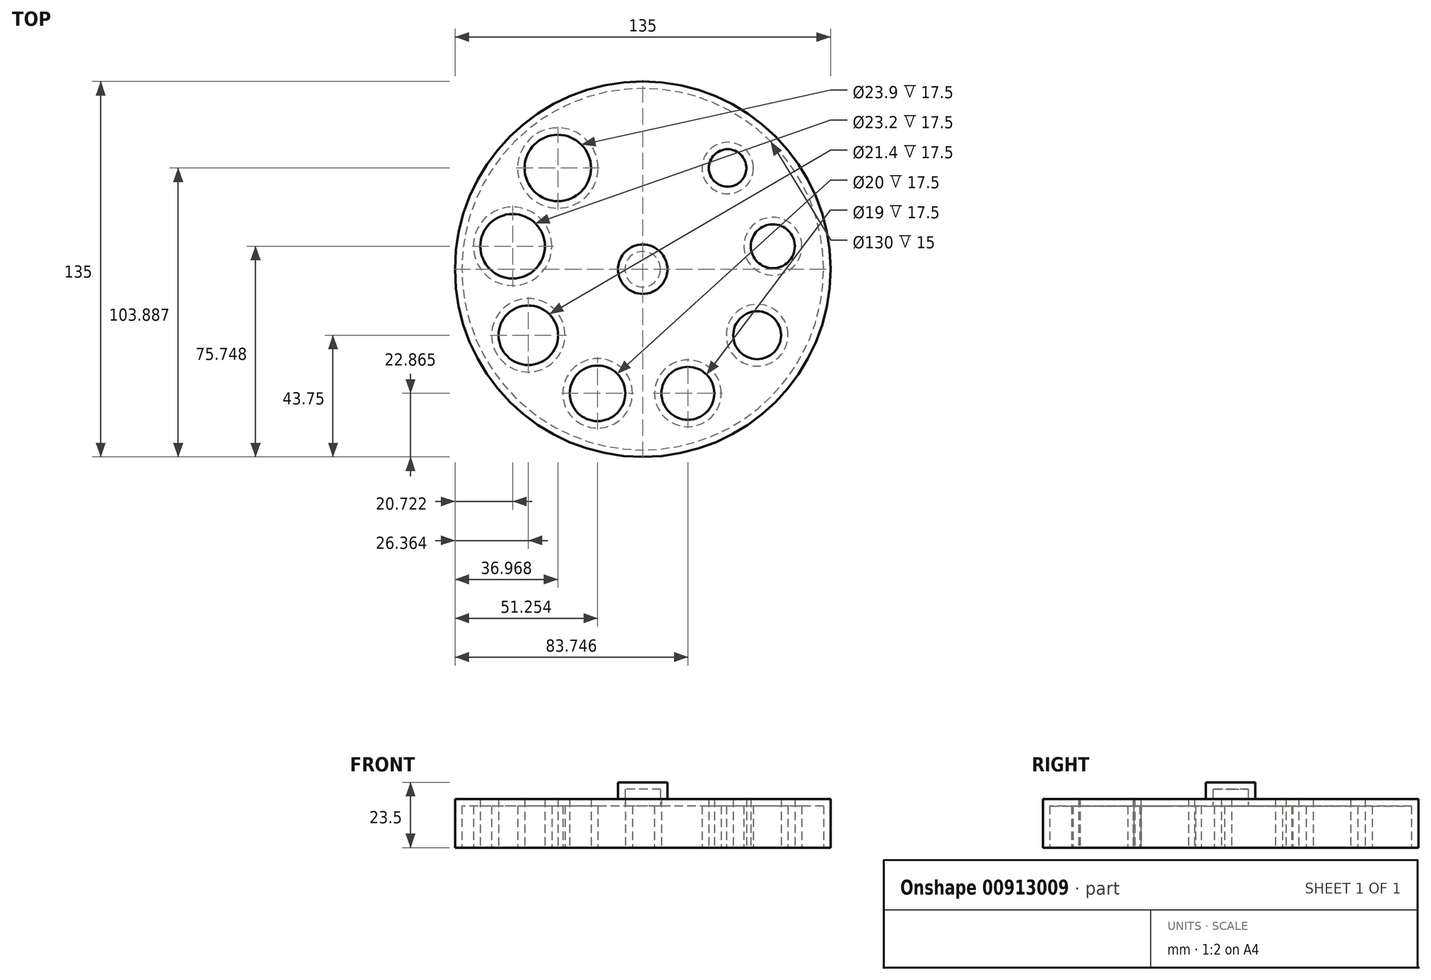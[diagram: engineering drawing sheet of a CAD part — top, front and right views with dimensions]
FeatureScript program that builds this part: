
annotation { "Feature Type Name" : "Feature", "Feature Type Description" : "" }
export const myFeature = defineFeature(function(context is Context, id is Id, definition is map)
    precondition{}
    {
        {
            var Q0;
            Q0=qCreatedBy(makeId("Top.planeOp"),FACE);
            var sketch = newSketch(context, id + "F0", { "sketchPlane" : qUnion([Q0])});
            skPoint(sketch, "E0", {"position": v(0, 47.5) * mm});
            skPoint(sketch, "E1.1.0", {"position": v(-30.53, 36.39) * mm});
            skPoint(sketch, "E1.2.0", {"position": v(-46.78, 8.25) * mm});
            skPoint(sketch, "E1.3.0", {"position": v(-41.14, -23.75) * mm});
            skPoint(sketch, "E1.4.0", {"position": v(-16.25, -44.64) * mm});
            skPoint(sketch, "E1.5.0", {"position": v(16.25, -44.64) * mm});
            skPoint(sketch, "E1.6.0", {"position": v(41.14, -23.75) * mm});
            skPoint(sketch, "E1.7.0", {"position": v(46.78, 8.25) * mm});
            skPoint(sketch, "E1.8.0", {"position": v(30.53, 36.39) * mm});
            skPoint(sketch, "E1.center", {"position": v(0, 0) * mm});
            skCircle(sketch, "E2", {"center": v(30.53, 36.39) * mm, "radius": 9.25 * mm});
            skCircle(sketch, "E3", {"center": v(46.78, 8.25) * mm, "radius": 10.4 * mm});
            skCircle(sketch, "E4", {"center": v(41.14, -23.75) * mm, "radius": 11.1 * mm});
            skCircle(sketch, "E5", {"center": v(16.25, -44.64) * mm, "radius": 12 * mm});
            skCircle(sketch, "E6", {"center": v(-16.25, -44.64) * mm, "radius": 12.5 * mm});
            skCircle(sketch, "E7", {"center": v(-41.14, -23.75) * mm, "radius": 13.2 * mm});
            skCircle(sketch, "E8", {"center": v(-46.78, 8.25) * mm, "radius": 14.1 * mm});
            skCircle(sketch, "E9", {"center": v(-30.53, 36.39) * mm, "radius": 14.45 * mm});
            skCircle(sketch, "E10", {"center": v(0, 0) * mm, "radius": 65 * mm});
            skCircle(sketch, "E11", {"center": v(0, 0) * mm, "radius": 6.38 * mm});
            skSolve(sketch);
        }
        {
            var Q0;
            Q0=makeQuery(id+"F0.imprint","IMPRINT",FACE,{"disambiguationData":[TD([[makeQuery(id+"F0.imprint","IMPRINT",EDGE,{"derivedFrom":sQuery(id+"F0.wireOp",EDGE,"E11")}),1.0]])]});
            extrude(context, id + "F1", {"entities" : qUnion([Q0]), "depth" : 21 * mm, "offsetDistance" : 25 * mm});
        }
        {
            var Q0;
            Q0=makeQuery(id+"F0.imprint","IMPRINT",FACE,{"disambiguationData":[TD([[makeQuery(id+"F0.imprint","IMPRINT",EDGE,{"derivedFrom":sQuery(id+"F0.wireOp",EDGE,"E2")}),-1.0]])]});
            extrude(context, id + "F2", {"entities" : qUnion([Q0]), "operationType" : NewBodyOperationType.ADD, "depth" : 15 * mm, "offsetDistance" : 25 * mm});
        }
        {
            var Q0;
            {var subQ0=sQuery(id+"F0.wireOp",EDGE,"E11");Q0=makeQuery(id+"F2.boolean.opBoolean","MERGE",FACE,{"derivedFrom":[makeQuery(id+"F1.opExtrude","CAP_FACE",FACE,{"disambiguationData":[OSD([subQ0])],"isStart":true}),makeQuery(id+"F2.opExtrude","CAP_FACE",FACE,{"disambiguationData":[OSD([sQuery(id+"F0.wireOp",EDGE,"E2"),sQuery(id+"F0.wireOp",EDGE,"E3"),sQuery(id+"F0.wireOp",EDGE,"E4"),sQuery(id+"F0.wireOp",EDGE,"E5"),sQuery(id+"F0.wireOp",EDGE,"E6"),sQuery(id+"F0.wireOp",EDGE,"E7"),sQuery(id+"F0.wireOp",EDGE,"E8"),sQuery(id+"F0.wireOp",EDGE,"E9"),sQuery(id+"F0.wireOp",EDGE,"E10"),subQ0])],"isStart":true})]});}
            shell(context, id + "F3", {"entities" : qUnion([Q0]), "thickness" : 2.5 * mm, "oppositeDirection" : true});
        }
    });
